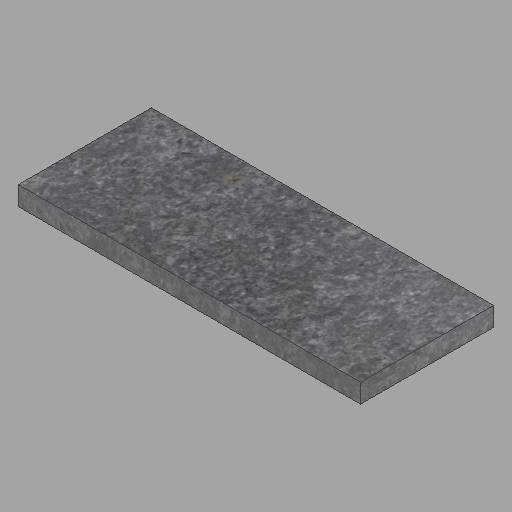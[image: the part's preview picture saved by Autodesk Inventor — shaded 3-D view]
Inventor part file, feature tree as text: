
AUTODESK INVENTOR PART (.ipt)
format: ipt  version: 2023 (Build 270158000, 158)  size: 221,696 bytes
history: native  units: in
note: dims shown in document units (in); Inventor stores cm internally (conversion verified against a paired STEP export)
features: extrude x1, sketch x1
ambient origin geometry x8: Origin, YZ Plane, XZ Plane, XY Plane, X Axis, Y Axis, Z Axis, Center Point
bodies: Solid1 (feature_tree)
feature tree (2):
  extrude  "Extrusion1"  Depth=14.0in
  sketch  "Sketch1"  dims[d0=2.0in d1=14.0in d2=36.0in d3=0.0in]
